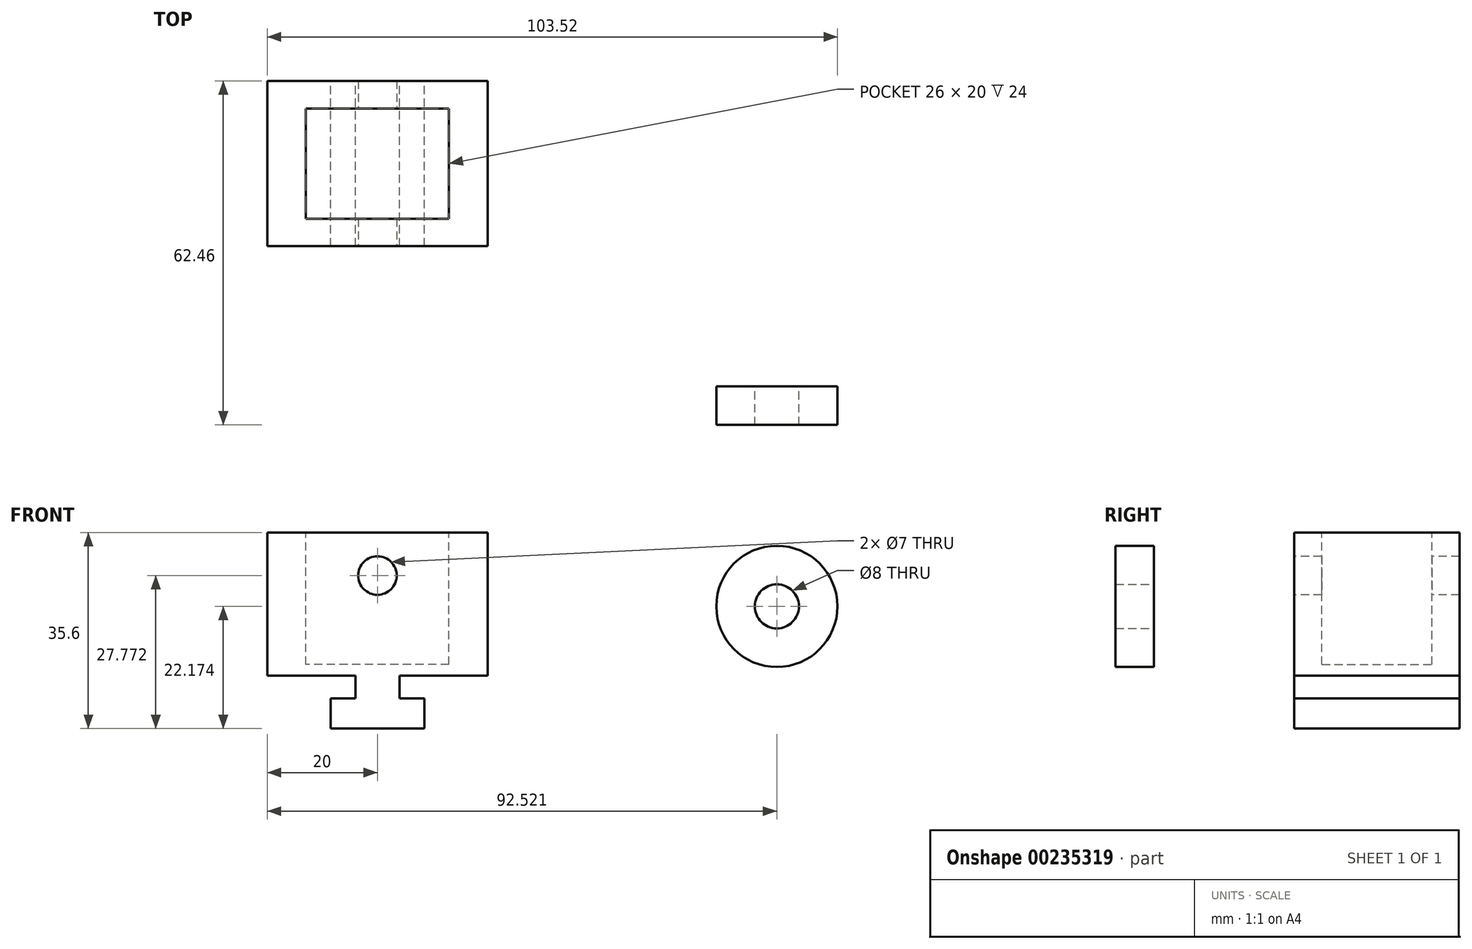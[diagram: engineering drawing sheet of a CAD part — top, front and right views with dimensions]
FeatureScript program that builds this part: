
annotation { "Feature Type Name" : "Feature", "Feature Type Description" : "" }
export const myFeature = defineFeature(function(context is Context, id is Id, definition is map)
    precondition{}
    {
        {
            var Q0;
            Q0=qCreatedBy(makeId("Top.planeOp"),FACE);
            var sketch = newSketch(context, id + "F0", { "sketchPlane" : qUnion([Q0])});
            skLineSegment(sketch, "E0.bottom", {"start": v(-31.06, 25.46) * mm, "end": v(-48.06, 25.46) * mm});
            skLineSegment(sketch, "E0.top", {"start": v(-31.06, 55.46) * mm, "end": v(-48.06, 55.46) * mm});
            skLineSegment(sketch, "E0.left", {"start": v(-31.06, 25.46) * mm, "end": v(-31.06, 55.46) * mm});
            skLineSegment(sketch, "E0.right", {"start": v(-48.06, 25.46) * mm, "end": v(-48.06, 55.46) * mm});
            skPoint(sketch, "E0.middle", {"position": v(-39.56, 40.46) * mm});
            skSolve(sketch);
        }
        {
            var Q0;
            Q0 = qSketchRegion(id + "F0", true);
            extrude(context, id + "F1", {"entities" : qUnion([Q0]), "depth" : 5.5 * mm});
        }
        {
            var Q0;
            Q0=makeQuery(id+"F1.opExtrude","CAP_FACE",FACE,{"disambiguationData":[OSD([sQuery(id+"F0.wireOp",EDGE,"E0.bottom"),sQuery(id+"F0.wireOp",EDGE,"E0.top"),sQuery(id+"F0.wireOp",EDGE,"E0.left"),sQuery(id+"F0.wireOp",EDGE,"E0.right")])],"isStart":false});
            var sketch = newSketch(context, id + "F2", { "sketchPlane" : qUnion([Q0])});
            skLineSegment(sketch, "E1.bottom", {"start": v(-35.56, 25.46) * mm, "end": v(-43.56, 25.46) * mm});
            skLineSegment(sketch, "E1.top", {"start": v(-35.56, 55.46) * mm, "end": v(-43.56, 55.46) * mm});
            skLineSegment(sketch, "E1.left", {"start": v(-35.56, 25.46) * mm, "end": v(-35.56, 55.46) * mm});
            skLineSegment(sketch, "E1.right", {"start": v(-43.56, 25.46) * mm, "end": v(-43.56, 55.46) * mm});
            skPoint(sketch, "E1.middle", {"position": v(-39.56, 40.46) * mm});
            skPoint(sketch, "E1.middle.positionSnap0", {"position": v(-31.06, 40.46) * mm});
            skPoint(sketch, "E1.middle.positionSnap1", {"position": v(-39.56, 55.46) * mm});
            skPoint(sketch, "E1.centerSnap0", {"position": v(-31.06, 40.46) * mm});
            skPoint(sketch, "E1.centerSnap1", {"position": v(-39.56, 55.46) * mm});
            skSolve(sketch);
        }
        {
            var Q0;
            Q0 = qSketchRegion(id + "F2", true);
            extrude(context, id + "F3", {"entities" : qUnion([Q0]), "operationType" : NewBodyOperationType.ADD, "depth" : 4.1 * mm});
        }
        {
            var Q0;
            Q0=makeQuery(id+"F3.opExtrude","CAP_FACE",FACE,{"disambiguationData":[OSD([sQuery(id+"F2.wireOp",EDGE,"E1.bottom"),sQuery(id+"F2.wireOp",EDGE,"E1.top"),sQuery(id+"F2.wireOp",EDGE,"E1.left"),sQuery(id+"F2.wireOp",EDGE,"E1.right")])],"isStart":false});
            var sketch = newSketch(context, id + "F4", { "sketchPlane" : qUnion([Q0])});
            skLineSegment(sketch, "E2.bottom", {"start": v(-19.56, 25.46) * mm, "end": v(-59.56, 25.46) * mm});
            skLineSegment(sketch, "E2.top", {"start": v(-19.56, 55.46) * mm, "end": v(-59.56, 55.46) * mm});
            skLineSegment(sketch, "E2.left", {"start": v(-19.56, 25.46) * mm, "end": v(-19.56, 55.46) * mm});
            skLineSegment(sketch, "E2.right", {"start": v(-59.56, 25.46) * mm, "end": v(-59.56, 55.46) * mm});
            skPoint(sketch, "E2.middle", {"position": v(-39.56, 40.46) * mm});
            skPoint(sketch, "E2.middle.positionSnap0", {"position": v(-39.56, 25.46) * mm});
            skPoint(sketch, "E2.middle.positionSnap1", {"position": v(-43.56, 40.46) * mm});
            skPoint(sketch, "E2.centerSnap0", {"position": v(-39.56, 25.46) * mm});
            skPoint(sketch, "E2.centerSnap1", {"position": v(-43.56, 40.46) * mm});
            skSolve(sketch);
        }
        {
            var Q0;
            Q0 = qSketchRegion(id + "F4", true);
            extrude(context, id + "F5", {"entities" : qUnion([Q0]), "operationType" : NewBodyOperationType.ADD, "depth" : 26 * mm});
        }
        {
            var Q0;
            Q0=makeQuery(id+"F5.opExtrude","CAP_FACE",FACE,{"disambiguationData":[OSD([sQuery(id+"F4.wireOp",EDGE,"E2.bottom"),sQuery(id+"F4.wireOp",EDGE,"E2.top"),sQuery(id+"F4.wireOp",EDGE,"E2.left"),sQuery(id+"F4.wireOp",EDGE,"E2.right")])],"isStart":false});
            var sketch = newSketch(context, id + "F6", { "sketchPlane" : qUnion([Q0])});
            skLineSegment(sketch, "E3.bottom", {"start": v(-26.56, 30.46) * mm, "end": v(-52.56, 30.46) * mm});
            skLineSegment(sketch, "E3.top", {"start": v(-26.56, 50.46) * mm, "end": v(-52.56, 50.46) * mm});
            skLineSegment(sketch, "E3.left", {"start": v(-26.56, 30.46) * mm, "end": v(-26.56, 50.46) * mm});
            skLineSegment(sketch, "E3.right", {"start": v(-52.56, 30.46) * mm, "end": v(-52.56, 50.46) * mm});
            skPoint(sketch, "E3.middle", {"position": v(-39.56, 40.46) * mm});
            skPoint(sketch, "E3.middle.positionSnap0", {"position": v(-19.56, 40.46) * mm});
            skPoint(sketch, "E3.middle.positionSnap1", {"position": v(-39.56, 55.46) * mm});
            skPoint(sketch, "E3.centerSnap0", {"position": v(-19.56, 40.46) * mm});
            skPoint(sketch, "E3.centerSnap1", {"position": v(-39.56, 55.46) * mm});
            skSolve(sketch);
        }
        {
            var Q0;
            Q0 = qSketchRegion(id + "F6", true);
            extrude(context, id + "F7", {"entities" : qUnion([Q0]), "operationType" : NewBodyOperationType.REMOVE, "oppositeDirection" : true, "depth" : 24 * mm});
        }
        {
            var Q0;
            Q0=makeQuery(id+"F5.boolean.opBoolean","MERGE",FACE,{"derivedFrom":[makeQuery(id+"F3.boolean.opBoolean","MERGE",FACE,{"derivedFrom":[makeQuery(id+"F1.opExtrude","SWEPT_FACE",FACE,{"disambiguationData":[OSD([sQuery(id+"F0.wireOp",EDGE,"E0.bottom")])]}),makeQuery(id+"F3.opExtrude","SWEPT_FACE",FACE,{"disambiguationData":[OSD([sQuery(id+"F2.wireOp",EDGE,"E1.bottom")])]})]}),makeQuery(id+"F5.opExtrude","SWEPT_FACE",FACE,{"disambiguationData":[OSD([sQuery(id+"F4.wireOp",EDGE,"E2.bottom")])]})]});
            var sketch = newSketch(context, id + "F8", { "sketchPlane" : qUnion([Q0])});
            skCircle(sketch, "E4", {"center": v(-39.56, 27.77) * mm, "radius": 3.5 * mm});
            skPoint(sketch, "E4.centerSnap0", {"position": v(-39.56, 35.6) * mm});
            skSolve(sketch);
        }
        {
            var Q0;
            Q0 = qSketchRegion(id + "F8", true);
            extrude(context, id + "F9", {"entities" : qUnion([Q0]), "operationType" : NewBodyOperationType.REMOVE, "endBound" : BoundingType.THROUGH_ALL, "oppositeDirection" : true, "depth" : 25 * mm});
        }
        {
            var Q0;
            Q0=qCreatedBy(makeId("Front.planeOp"),FACE);
            var sketch = newSketch(context, id + "F10", { "sketchPlane" : qUnion([Q0])});
            skCircle(sketch, "E5", {"center": v(32.96, 22.17) * mm, "radius": 11 * mm});
            skCircle(sketch, "E6", {"center": v(32.96, 22.17) * mm, "radius": 4 * mm});
            skSolve(sketch);
        }
        {
            var Q0;
            Q0 = qSketchRegion(id + "F10", true);
            extrude(context, id + "F11", {"entities" : qUnion([Q0]), "depth" : 7 * mm});
        }
    });
